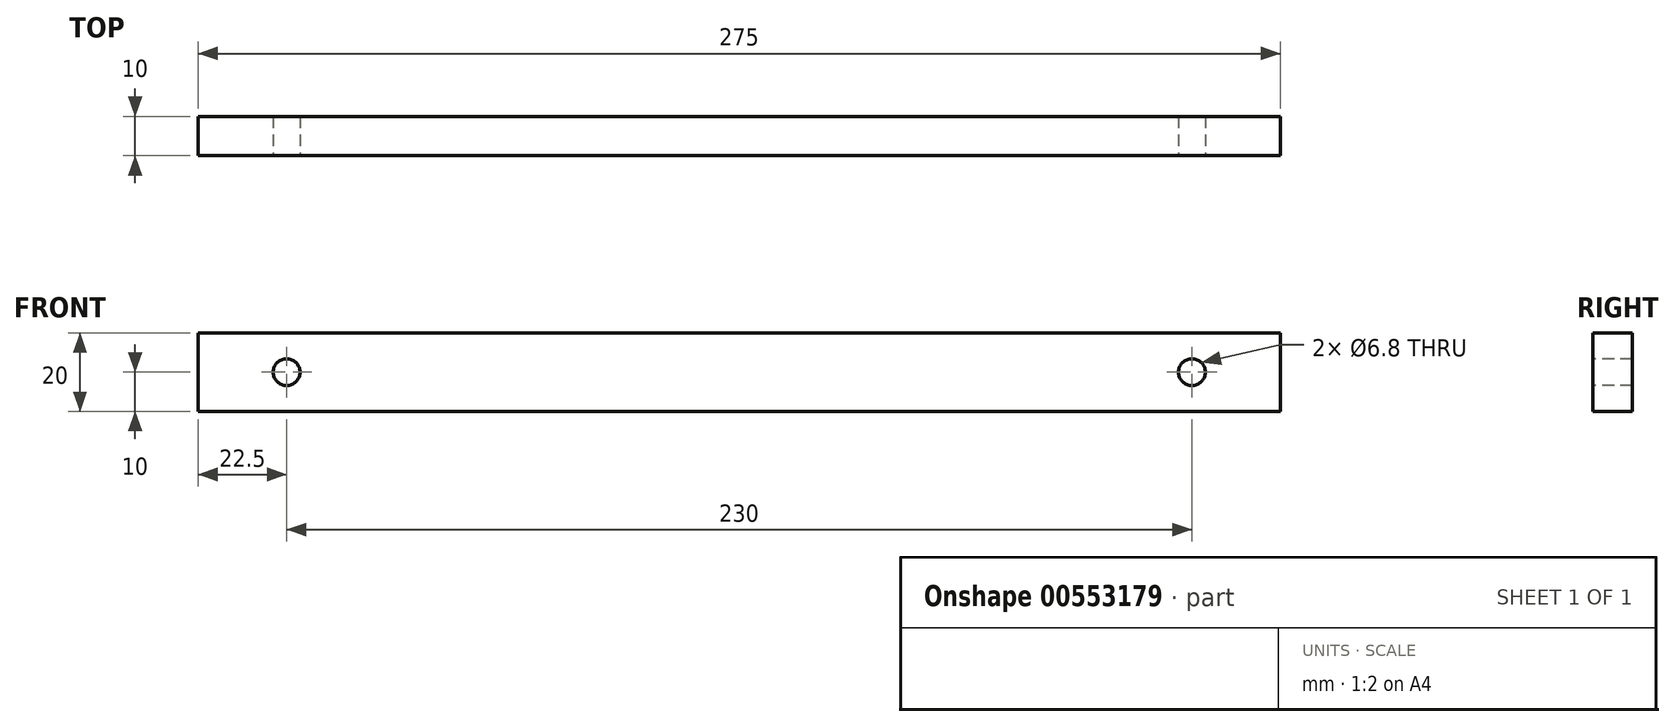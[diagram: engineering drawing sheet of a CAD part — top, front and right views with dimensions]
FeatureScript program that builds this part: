
annotation { "Feature Type Name" : "Feature", "Feature Type Description" : "" }
export const myFeature = defineFeature(function(context is Context, id is Id, definition is map)
    precondition{}
    {
        {
            var Q0;
            Q0=qCreatedBy(makeId("Front.planeOp"),FACE);
            var sketch = newSketch(context, id + "F0", { "sketchPlane" : qUnion([Q0])});
            skLineSegment(sketch, "E0.bottom", {"start": v(137.5, 10) * mm, "end": v(-137.5, 10) * mm});
            skLineSegment(sketch, "E0.top", {"start": v(137.5, -10) * mm, "end": v(-137.5, -10) * mm});
            skLineSegment(sketch, "E0.left", {"start": v(137.5, 10) * mm, "end": v(137.5, -10) * mm});
            skLineSegment(sketch, "E0.right", {"start": v(-137.5, 10) * mm, "end": v(-137.5, -10) * mm});
            skPoint(sketch, "E0.middle", {"position": v(0, 0) * mm});
            skLineSegment(sketch, "E1", {"start": v(-144.81, 0) * mm, "end": v(152.27, 0) * mm, "construction": true});
            skPoint(sketch, "E1.startSnap0", {"position": v(-137.5, 0) * mm});
            skPoint(sketch, "E1.endSnap0", {"position": v(-137.5, 0) * mm});
            skSolve(sketch);
        }
        {
            var Q0;
            Q0 = qSketchRegion(id + "F0", true);
            extrude(context, id + "F1", {"entities" : qUnion([Q0]), "depth" : 10 * mm, "offsetDistance" : 25 * mm});
        }
        {
            var Q0;
            Q0=makeQuery(id+"F1.opExtrude","CAP_FACE",FACE,{"disambiguationData":[OSD([sQuery(id+"F0.wireOp",EDGE,"E0.bottom"),sQuery(id+"F0.wireOp",EDGE,"E0.top"),sQuery(id+"F0.wireOp",EDGE,"E0.left"),sQuery(id+"F0.wireOp",EDGE,"E0.right")])],"isStart":false});
            var sketch = newSketch(context, id + "F2", { "sketchPlane" : qUnion([Q0])});
            skPoint(sketch, "E2", {"position": v(-115, 0) * mm});
            skPoint(sketch, "E2.positionSnap0", {"position": v(-137.5, 0) * mm});
            skPoint(sketch, "E3", {"position": v(115, 0) * mm});
            skSolve(sketch);
        }
        {
            var Q0;
            Q0=sQuery(id+"F2.wireOp",VERTEX,"E2");
            var Q1;
            Q1=sQuery(id+"F2.wireOp",VERTEX,"E3");
            var Q2;
            Q2=makeQuery(id+"F1.opExtrude","SWEPT_BODY",BODY,{"disambiguationData":[OSD([sQuery(id+"F0.wireOp",EDGE,"E0.bottom"),sQuery(id+"F0.wireOp",EDGE,"E0.top"),sQuery(id+"F0.wireOp",EDGE,"E0.left"),sQuery(id+"F0.wireOp",EDGE,"E0.right")])]});
            hole(context, id + "F3", {"style" : HoleStyle.SIMPLE, "endStyle" : HoleEndStyle.THROUGH, "standardTappedOrClearance" : lookupTablePath({ "standard" : "ISO", "engagement" : "75%", "pitch" : "1.25 mm", "size" : "M8", "type" : "Tapped" }), "standardBlindInLast" : lookupTablePath({ "standard" : "ISO", "engagement" : "75%", "pitch" : "1.25 mm", "size" : "M8", "type" : "Tapped" }), "holeDiameter" : 6.8 * mm, "showTappedDepth" : true, "isTappedThrough" : true, "tappedDepth" : 12 * mm, "tapClearance" : 3, "locations" : qUnion([Q0, Q1]), "scope" : qUnion([Q2]), "majorDiameter" : 8 * mm});
        }
    });
